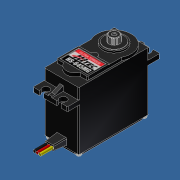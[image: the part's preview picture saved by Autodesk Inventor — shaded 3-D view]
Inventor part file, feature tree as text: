
AUTODESK INVENTOR PART (.ipt)
format: ipt  version: unknown  size: 757,248 bytes
history: native  units: mm
features: sketch x17, extrude x15, fillet x4, chamfer x2, other x2, plane x1, mirror x1, pattern_circular x1, thread x1, revolve x1, pattern_linear x1
ambient origin geometry x8: Origin, YZ Plane, XZ Plane, XY Plane, X Axis, Y Axis, Z Axis, Center Point
bodies: Solid1 (feature_tree)
feature tree (46):
  extrude  "Extrusion1"  Depth=9.9mm
  extrude  "Extrusion2"  Depth=20.15mm
  fillet  "Fillet1"  Radius=35.25mm
  extrude  "Extrusion3"  Depth=17.75mm
  plane  "Work Plane1"
  extrude  "Extrusion4"  Depth=34.3mm
  extrude  "Extrusion5"  Depth=1.966646mm
  mirror  "Mirror1"
  extrude  "Extrusion6"  Depth=1.75mm TaperAngle=0.0deg
  extrude  "Extrusion7"  Depth=12.8mm
  extrude  "Extrusion8"  Depth=3.6mm
  extrude  "Extrusion9"  Depth=1.0mm
  pattern_circular  "Circular Pattern1"  [2 undecoded]
  extrude  "Extrusion10"  Depth=1.25mm
  chamfer  "Chamfer1"  Distance=24.15mm
  thread  "Thread1"  [1 undecoded]
  revolve  "Revolution1"  [1 undecoded]
  chamfer  "Chamfer2"  Distance=0.740982mm
  fillet  "Fillet2"  Radius=27.036082mm
  extrude  "Extrusion11"  Depth=2.0mm TaperAngle=0.0deg
  extrude  "Extrusion12"  Depth=13.0mm
  fillet  "Fillet3"  Radius=1.0mm
  extrude  "Extrusion13"  Depth=11.2mm
  pattern_linear  "Rectangular Pattern1"  Spacing1=0.26mm  [1 undecoded]
  extrude  "Extrusion14"  Depth=5.8mm
  fillet  "Fillet4"  Radius=5.2mm
  extrude  "Extrusion15"  Depth=3.6mm TaperAngle=0.0deg
  other  "Decal1"
  sketch  "Sketch1"  dims[d0=19.8mm d1=9.9mm]
  sketch  "Sketch2"  dims[d2=40.3mm d3=20.15mm d4=35.25mm d5=0.0mm]
  sketch  "Sketch3"  dims[d6=10.0mm d7=17.75mm]
  sketch  "Sketch4"  dims[d8=8.875mm d9=34.3mm]
  sketch  "Sketch5"  dims[d10=4.8mm d11=1.966646mm]
  sketch  "Sketch6"  dims[d12=10.249769mm d13=1.75mm d14=0.0mm]
  sketch  "Sketch7"  dims[d15=0.5mm d16=12.8mm]
  sketch  "Sketch8"  dims[d17=0.5mm d18=3.6mm]
  sketch  "Sketch9"  dims[d19=1.0mm d20=1.0mm]
  sketch  "Sketch10"  dims[d21=1.0mm]
  sketch  "Sketch11"  dims[d22=1.0mm]
  sketch  "Sketch12"  dims[d23=0.3mm d24=0.0mm]
  sketch  "Sketch13"  dims[d25=-8.8mm]
  sketch  "Sketch14"  dims[d26=6.5mm d27=6.5mm]
  sketch  "Sketch15"  dims[d28=4.0mm]
  sketch  "Sketch16"  dims[d29=2.5mm]
  sketch  "Sketch17"  dims[d31=5.0mm d32=2.5mm d33=1.25mm d34=24.15mm d35=2.5mm d36=0.0mm d37=1.85575mm d38=0.740982mm d39=27.036082mm d40=2.0mm d41=0.0mm d42=13.0mm d43=1.0mm d44=0.0mm d45=11.2mm d46=0.26mm d47=0.0mm d48=5.8mm d49=5.2mm d50=3.6mm d51=0.0mm d52=0.4mm d53=4.363323mm d54=3.6mm d55=0.0mm d56=300.0mm d57=360.0deg d59=0.189756mm d60=0.189756mm d61=1.9mm d62=3.0mm d63=0.0mm d64=0.3mm d65=2.0mm d66=45.0deg d67=10.0mm d68=0.0mm d69=90.0deg d70=1.0mm d71=2.0mm d72=60.0deg d73=0.5mm d74=3.6mm d75=8.6mm d76=18.8mm d77=1.7mm d78=0.0mm d79=1.5mm d80=0.0mm d81=0.5mm d82=0.2mm d83=0.2mm d84=0.9mm d85=0.9mm d86=0.7mm d87=0.0mm d88=20.0mm d90=17.1mm d91=20.0mm d93=37.6mm d94=4.0mm d95=6.0mm d96=3.0mm d97=1.0mm d98=7.0mm d99=-0.698132mm d100=0.5mm d101=1.6mm d102=1.6mm d103=1.6mm d104=1.6mm d105=1.6mm d106=7.0mm d107=0.0mm]
  other  "Image1"
note: 5 required parameter values undecoded (feature->parameter linkage not recoverable at this tier; creation-order binding heuristic only, values carry confidence <= 0.55)